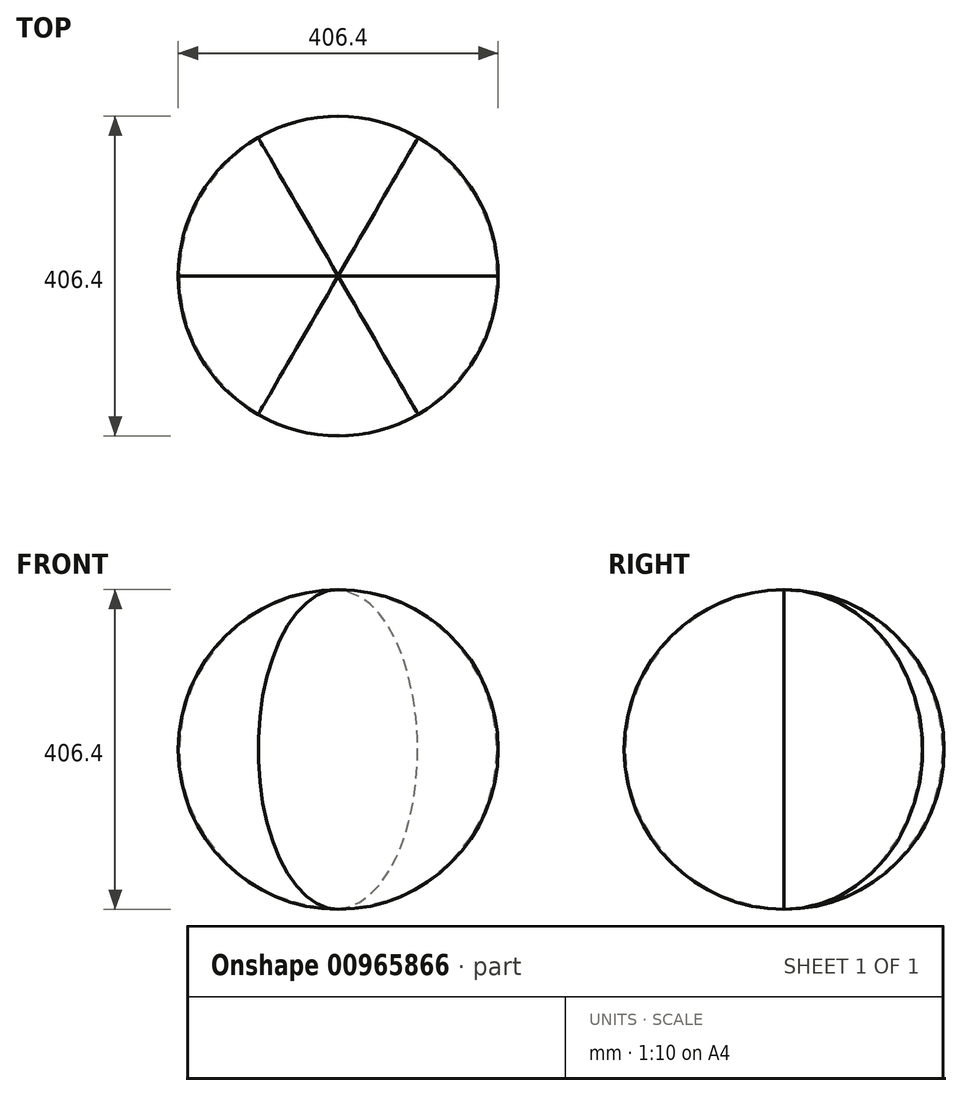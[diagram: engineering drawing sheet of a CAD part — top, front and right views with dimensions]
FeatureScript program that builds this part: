
annotation { "Feature Type Name" : "Feature", "Feature Type Description" : "" }
export const myFeature = defineFeature(function(context is Context, id is Id, definition is map)
    precondition{}
    {
        {
            var Q0;
            Q0=qCreatedBy(makeId("Front.planeOp"),FACE);
            var sketch = newSketch(context, id + "F0", { "sketchPlane" : qUnion([Q0])});
            skArc(sketch, "E0", {"start": v(0, -203.2) * mm, "mid": v(203.2, 0) * mm, "end": v(0, 203.2) * mm});
            skLineSegment(sketch, "E1", {"start": v(0, 203.2) * mm, "end": v(0, -203.2) * mm});
            skArc(sketch, "E2", {"start": v(0, -201.61) * mm, "mid": v(201.61, 0) * mm, "end": v(0, 201.61) * mm});
            skSolve(sketch);
        }
        {
            var Q0;
            {var subQ0=sQuery(id+"F0.wireOp",EDGE,"E0");Q0=makeQuery(id+"F0.imprint","IMPRINT",FACE,{"disambiguationData":[TD([[makeQuery(id+"F0.imprint","IMPRINT",EDGE,{"derivedFrom":subQ0}),1.0]])]});}
            var Q1;
            Q1=sQuery(id+"F0.wireOp",EDGE,"E1");
            revolve(context, id + "F1", {"surfaceOperationType" : NewSurfaceOperationType.NEW, "entities" : qUnion([Q0]), "axis" : qUnion([Q1]), "revolveType" : RevolveType.ONE_DIRECTION, "angle" : 60 * degree});
        }
        {
            var Q0;
            Q0=qCreatedBy(makeId("Right.planeOp"),FACE);
            var sketch = newSketch(context, id + "F2", { "sketchPlane" : qUnion([Q0])});
            skLineSegment(sketch, "E3", {"start": v(0, 204.27) * mm, "end": v(0, -201.72) * mm});
            skSolve(sketch);
        }
        {
            var Q0;
            Q0=makeQuery(id+"F1.opRevolve","SWEPT_BODY",BODY,{"disambiguationData":[OSD([sQuery(id+"F0.wireOp",EDGE,"E0"),sQuery(id+"F0.wireOp",EDGE,"E1"),sQuery(id+"F0.wireOp",EDGE,"E2")])]});
            var Q1;
            Q1=sQuery(id+"F2.wireOp",EDGE,"E3");
            circularPattern(context, id + "F3", {"entities" : qUnion([Q0]), "axis" : qUnion([Q1]), "angle" : 360 * degree, "instanceCount" : 6, "equalSpace" : true});
        }
    });
